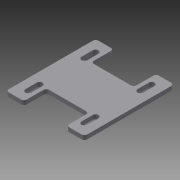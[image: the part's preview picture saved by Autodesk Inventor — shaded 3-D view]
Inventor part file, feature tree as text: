
AUTODESK INVENTOR PART (.ipt)
format: ipt  version: 2013 (Build 170138000, 138)  size: 127,488 bytes
history: native  units: in
note: dims shown in document units (in); Inventor stores cm internally (conversion verified against a paired STEP export)
features: extrude x1, fillet x1, mirror x1, sketch x1
ambient origin geometry x8: Origin, YZ Plane, XZ Plane, XY Plane, X Axis, Y Axis, Z Axis, Center Point
bodies: Solid1 (feature_tree)
feature tree (4):
  extrude  "Extrusion1"  Depth=0.1875in TaperAngle=0.0deg
  fillet  "Fillet1"  Radius=1.75in
  mirror  "Mirror2"
  sketch  "Sketch1"  dims[d1=4.0in d6=0.1875in d7=0.0in d8=1.75in d11=0.26in d14=0.5in d15=0.5in d18=0.5in d19=0.8in d20=0.125in d21=1.25in d23=2.0in d24=1.0in d25=2.5in d26=0.26in]
